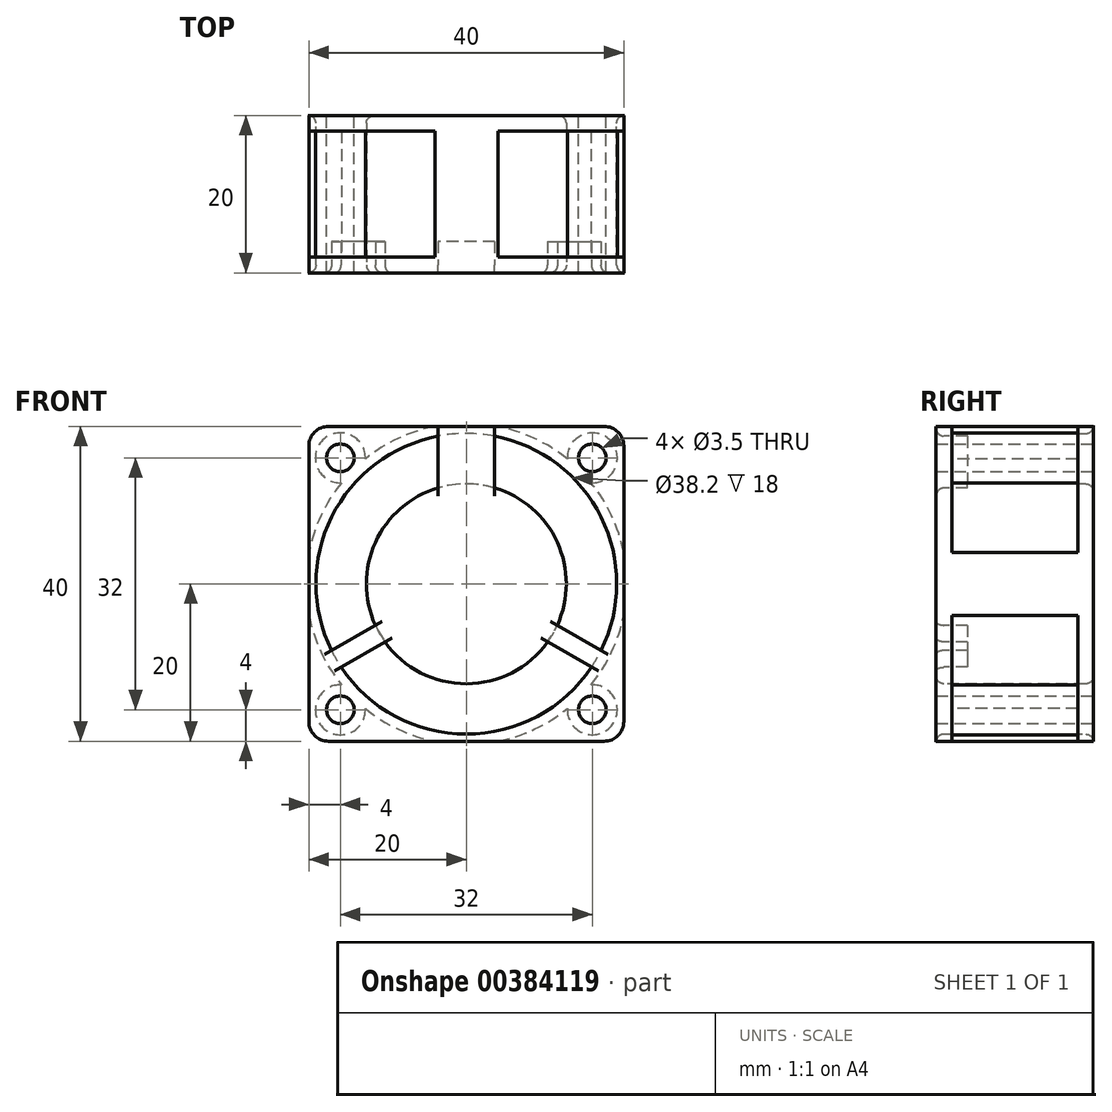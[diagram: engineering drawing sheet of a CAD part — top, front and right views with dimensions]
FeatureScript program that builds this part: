
annotation { "Feature Type Name" : "Feature", "Feature Type Description" : "" }
export const myFeature = defineFeature(function(context is Context, id is Id, definition is map)
    precondition{}
    {
        {
            var Q0;
            Q0=qCreatedBy(makeId("Front.planeOp"),FACE);
            var sketch = newSketch(context, id + "F0", { "sketchPlane" : qUnion([Q0])});
            skLineSegment(sketch, "E0.bottom", {"start": v(-20, 20) * mm, "end": v(20, 20) * mm});
            skLineSegment(sketch, "E0.top", {"start": v(-20, -20) * mm, "end": v(20, -20) * mm});
            skLineSegment(sketch, "E0.left", {"start": v(-20, 20) * mm, "end": v(-20, -20) * mm});
            skLineSegment(sketch, "E0.right", {"start": v(20, 20) * mm, "end": v(20, -20) * mm});
            skLineSegment(sketch, "E1", {"start": v(0, 22.42) * mm, "end": v(0, -25.75) * mm, "construction": true});
            skLineSegment(sketch, "E2", {"start": v(-21.61, 0) * mm, "end": v(23.43, 0) * mm, "construction": true});
            skLineSegment(sketch, "E3", {"start": v(-20.42, 20.42) * mm, "end": v(24.04, -24.04) * mm, "construction": true});
            skLineSegment(sketch, "E4", {"start": v(22.41, 22.41) * mm, "end": v(-20.4, -20.4) * mm, "construction": true});
            skCircle(sketch, "E5", {"center": v(-16, 16) * mm, "radius": 1.75 * mm});
            skCircle(sketch, "E6", {"center": v(16, 16) * mm, "radius": 1.75 * mm});
            skCircle(sketch, "E7", {"center": v(16, -16) * mm, "radius": 1.75 * mm});
            skCircle(sketch, "E8", {"center": v(-16, -16) * mm, "radius": 1.75 * mm});
            skCircle(sketch, "E9", {"center": v(0, 0) * mm, "radius": 19.1 * mm});
            skSolve(sketch);
        }
        {
            var Q0;
            Q0=qSketchRegion(id+"F0",true);
            extrude(context, id + "F1", {"entities" : qUnion([Q0]), "offsetDistance" : 25 * mm, "depth" : 20 * mm, "symmetric" : true});
        }
        {
            var Q0;
            Q0=qCreatedBy(makeId("Front.planeOp"),FACE);
            var sketch = newSketch(context, id + "F2", { "sketchPlane" : qUnion([Q0])});
            skArc(sketch, "E10", {"start": v(-12.83, 15.86) * mm, "mid": v(-18.25, 18.25) * mm, "end": v(-15.86, 12.83) * mm});
            skArc(sketch, "E11", {"start": v(-15.86, 12.83) * mm, "mid": v(-18.46, 8.67) * mm, "end": v(-20, 4) * mm});
            skLineSegment(sketch, "E12", {"start": v(20.4, 20.4) * mm, "end": v(4, 20.4) * mm});
            skLineSegment(sketch, "E13", {"start": v(-20.4, 20.4) * mm, "end": v(-20.4, 4) * mm});
            skLineSegment(sketch, "E14", {"start": v(-20.4, -20.4) * mm, "end": v(-4, -20.4) * mm});
            skLineSegment(sketch, "E15", {"start": v(20.4, -20.4) * mm, "end": v(20.4, -4) * mm});
            skArc(sketch, "E16", {"start": v(15.86, 12.83) * mm, "mid": v(18.25, 18.25) * mm, "end": v(12.83, 15.86) * mm});
            skArc(sketch, "E17", {"start": v(12.83, -15.86) * mm, "mid": v(18.25, -18.25) * mm, "end": v(15.86, -12.83) * mm});
            skArc(sketch, "E18", {"start": v(-15.86, -12.83) * mm, "mid": v(-18.25, -18.25) * mm, "end": v(-12.83, -15.86) * mm});
            skArc(sketch, "E19.trimOffspring", {"start": v(12.83, 15.86) * mm, "mid": v(8.67, 18.46) * mm, "end": v(4, 20) * mm});
            skArc(sketch, "E20.trimOffspring", {"start": v(15.86, -12.83) * mm, "mid": v(18.46, -8.67) * mm, "end": v(20, -4) * mm});
            skArc(sketch, "E21.trimOffspring", {"start": v(-12.83, -15.86) * mm, "mid": v(-8.67, -18.46) * mm, "end": v(-4, -20) * mm});
            skLineSegment(sketch, "E22", {"start": v(-20, 4) * mm, "end": v(-20.4, 4) * mm});
            skLineSegment(sketch, "E23", {"start": v(-20, -4) * mm, "end": v(-20.4, -4) * mm});
            skLineSegment(sketch, "E24", {"start": v(20, -4) * mm, "end": v(20.4, -4) * mm});
            skLineSegment(sketch, "E25", {"start": v(-4, -20) * mm, "end": v(-4, -20.4) * mm});
            skArc(sketch, "E26.trimOffspring", {"start": v(-20, -4) * mm, "mid": v(-18.46, -8.67) * mm, "end": v(-15.86, -12.83) * mm});
            skLineSegment(sketch, "E27.trimOffspring", {"start": v(-20.4, -4) * mm, "end": v(-20.4, -20.4) * mm});
            skLineSegment(sketch, "E28.trimOffspring", {"start": v(4, -20.4) * mm, "end": v(20.4, -20.4) * mm});
            skArc(sketch, "E29.trimOffspring", {"start": v(4, -20) * mm, "mid": v(8.67, -18.46) * mm, "end": v(12.83, -15.86) * mm});
            skLineSegment(sketch, "E30.trimOffspring", {"start": v(20.4, 4) * mm, "end": v(20.4, 20.4) * mm});
            skArc(sketch, "E31.trimOffspring", {"start": v(20, 4) * mm, "mid": v(18.46, 8.67) * mm, "end": v(15.86, 12.83) * mm});
            skLineSegment(sketch, "E32.trimOffspring", {"start": v(-4, 20.4) * mm, "end": v(-20.4, 20.4) * mm});
            skArc(sketch, "E33.trimOffspring", {"start": v(-4, 20) * mm, "mid": v(-8.67, 18.46) * mm, "end": v(-12.83, 15.86) * mm});
            skLineSegment(sketch, "E34", {"start": v(4, 20.4) * mm, "end": v(4, 20) * mm});
            skLineSegment(sketch, "E35", {"start": v(-4, 20.4) * mm, "end": v(-4, 20) * mm});
            skLineSegment(sketch, "E36", {"start": v(20, 4) * mm, "end": v(20.4, 4) * mm});
            skLineSegment(sketch, "E37", {"start": v(4, -20.4) * mm, "end": v(4, -20) * mm});
            skSolve(sketch);
        }
        {
            var Q0;
            Q0=qSketchRegion(id+"F2",true);
            extrude(context, id + "F3", {"entities" : qUnion([Q0]), "operationType" : NewBodyOperationType.REMOVE, "oppositeDirection" : true, "offsetDistance" : 25 * mm, "depth" : 16 * mm, "symmetric" : true});
        }
        {
            var Q0;
            {var subQ0=sQuery(id+"F0.wireOp",EDGE,"E0.bottom");var subQ1=sQuery(id+"F0.wireOp",EDGE,"E0.right");Q0=makeQuery(id+"F3.boolean.opBoolean","SPLIT",EDGE,{"disambiguationData":[TD([makeQuery(id+"F3.opExtrude","CAP_FACE",FACE,{"disambiguationData":[OSD([sQuery(id+"F2.wireOp",EDGE,"E12"),sQuery(id+"F2.wireOp",EDGE,"E16"),sQuery(id+"F2.wireOp",EDGE,"E19.trimOffspring"),sQuery(id+"F2.wireOp",EDGE,"5qj6X1HE-5dRS-yjT4-1pPR-XCu9oSXyVZGm"),sQuery(id+"F2.wireOp",EDGE,"E24"),sQuery(id+"F2.wireOp",EDGE,"E30.trimOffspring"),sQuery(id+"F2.wireOp",EDGE,"E31.trimOffspring")])],"isStart":true})])],"derivedFrom":makeQuery(id+"F1.opExtrude","SWEPT_EDGE",EDGE,{"disambiguationData":[OSD([subQ0,subQ1])]})});}
            var Q1;
            {var subQ0=sQuery(id+"F0.wireOp",EDGE,"E0.bottom");var subQ1=sQuery(id+"F0.wireOp",EDGE,"E0.right");Q1=makeQuery(id+"F3.boolean.opBoolean","SPLIT",EDGE,{"disambiguationData":[TD([makeQuery(id+"F3.opExtrude","CAP_FACE",FACE,{"disambiguationData":[OSD([sQuery(id+"F2.wireOp",EDGE,"E12"),sQuery(id+"F2.wireOp",EDGE,"E16"),sQuery(id+"F2.wireOp",EDGE,"E19.trimOffspring"),sQuery(id+"F2.wireOp",EDGE,"5qj6X1HE-5dRS-yjT4-1pPR-XCu9oSXyVZGm"),sQuery(id+"F2.wireOp",EDGE,"E24"),sQuery(id+"F2.wireOp",EDGE,"E30.trimOffspring"),sQuery(id+"F2.wireOp",EDGE,"E31.trimOffspring")])],"isStart":false})])],"derivedFrom":makeQuery(id+"F1.opExtrude","SWEPT_EDGE",EDGE,{"disambiguationData":[OSD([subQ0,subQ1])]})});}
            var Q2;
            {var subQ0=sQuery(id+"F0.wireOp",EDGE,"E0.right");var subQ1=sQuery(id+"F0.wireOp",EDGE,"E0.top");Q2=makeQuery(id+"F3.boolean.opBoolean","SPLIT",EDGE,{"disambiguationData":[TD([makeQuery(id+"F3.opExtrude","CAP_FACE",FACE,{"disambiguationData":[OSD([sQuery(id+"F2.wireOp",EDGE,"E15"),sQuery(id+"F2.wireOp",EDGE,"E17"),sQuery(id+"F2.wireOp",EDGE,"E20.trimOffspring"),sQuery(id+"F2.wireOp",EDGE,"E24"),sQuery(id+"F2.wireOp",EDGE,"E25"),sQuery(id+"F2.wireOp",EDGE,"E28.trimOffspring"),sQuery(id+"F2.wireOp",EDGE,"E29.trimOffspring")])],"isStart":true})])],"derivedFrom":makeQuery(id+"F1.opExtrude","SWEPT_EDGE",EDGE,{"disambiguationData":[OSD([subQ1,subQ0])]})});}
            var Q3;
            {var subQ0=sQuery(id+"F0.wireOp",EDGE,"E0.right");var subQ1=sQuery(id+"F0.wireOp",EDGE,"E0.top");Q3=makeQuery(id+"F3.boolean.opBoolean","SPLIT",EDGE,{"disambiguationData":[TD([makeQuery(id+"F3.opExtrude","CAP_FACE",FACE,{"disambiguationData":[OSD([sQuery(id+"F2.wireOp",EDGE,"E15"),sQuery(id+"F2.wireOp",EDGE,"E17"),sQuery(id+"F2.wireOp",EDGE,"E20.trimOffspring"),sQuery(id+"F2.wireOp",EDGE,"E24"),sQuery(id+"F2.wireOp",EDGE,"E25"),sQuery(id+"F2.wireOp",EDGE,"E28.trimOffspring"),sQuery(id+"F2.wireOp",EDGE,"E29.trimOffspring")])],"isStart":false})])],"derivedFrom":makeQuery(id+"F1.opExtrude","SWEPT_EDGE",EDGE,{"disambiguationData":[OSD([subQ1,subQ0])]})});}
            var Q4;
            {var subQ0=sQuery(id+"F0.wireOp",EDGE,"E0.bottom");var subQ1=sQuery(id+"F0.wireOp",EDGE,"E0.left");Q4=makeQuery(id+"F3.boolean.opBoolean","SPLIT",EDGE,{"disambiguationData":[TD([makeQuery(id+"F3.opExtrude","CAP_FACE",FACE,{"disambiguationData":[OSD([sQuery(id+"F2.wireOp",EDGE,"E10"),sQuery(id+"F2.wireOp",EDGE,"E11"),sQuery(id+"F2.wireOp",EDGE,"E13"),sQuery(id+"F2.wireOp",EDGE,"pvrkBk7z-V1rM-OS9Q-dIUC-16UQzA1z2bkd"),sQuery(id+"F2.wireOp",EDGE,"E22"),sQuery(id+"F2.wireOp",EDGE,"E32.trimOffspring"),sQuery(id+"F2.wireOp",EDGE,"E33.trimOffspring")])],"isStart":true})])],"derivedFrom":makeQuery(id+"F1.opExtrude","SWEPT_EDGE",EDGE,{"disambiguationData":[OSD([subQ0,subQ1])]})});}
            var Q5;
            {var subQ0=sQuery(id+"F0.wireOp",EDGE,"E0.bottom");var subQ1=sQuery(id+"F0.wireOp",EDGE,"E0.left");Q5=makeQuery(id+"F3.boolean.opBoolean","SPLIT",EDGE,{"disambiguationData":[TD([makeQuery(id+"F3.opExtrude","CAP_FACE",FACE,{"disambiguationData":[OSD([sQuery(id+"F2.wireOp",EDGE,"E10"),sQuery(id+"F2.wireOp",EDGE,"E11"),sQuery(id+"F2.wireOp",EDGE,"E13"),sQuery(id+"F2.wireOp",EDGE,"pvrkBk7z-V1rM-OS9Q-dIUC-16UQzA1z2bkd"),sQuery(id+"F2.wireOp",EDGE,"E22"),sQuery(id+"F2.wireOp",EDGE,"E32.trimOffspring"),sQuery(id+"F2.wireOp",EDGE,"E33.trimOffspring")])],"isStart":false})])],"derivedFrom":makeQuery(id+"F1.opExtrude","SWEPT_EDGE",EDGE,{"disambiguationData":[OSD([subQ0,subQ1])]})});}
            var Q6;
            {var subQ0=sQuery(id+"F0.wireOp",EDGE,"E0.left");var subQ1=sQuery(id+"F0.wireOp",EDGE,"E0.top");Q6=makeQuery(id+"F3.boolean.opBoolean","SPLIT",EDGE,{"disambiguationData":[TD([makeQuery(id+"F3.opExtrude","CAP_FACE",FACE,{"disambiguationData":[OSD([sQuery(id+"F2.wireOp",EDGE,"E14"),sQuery(id+"F2.wireOp",EDGE,"E18"),sQuery(id+"F2.wireOp",EDGE,"E21.trimOffspring"),sQuery(id+"F2.wireOp",EDGE,"E23"),sQuery(id+"F2.wireOp",EDGE,"E25"),sQuery(id+"F2.wireOp",EDGE,"E26.trimOffspring"),sQuery(id+"F2.wireOp",EDGE,"E27.trimOffspring")])],"isStart":false})])],"derivedFrom":makeQuery(id+"F1.opExtrude","SWEPT_EDGE",EDGE,{"disambiguationData":[OSD([subQ1,subQ0])]})});}
            var Q7;
            {var subQ0=sQuery(id+"F0.wireOp",EDGE,"E0.left");var subQ1=sQuery(id+"F0.wireOp",EDGE,"E0.top");Q7=makeQuery(id+"F3.boolean.opBoolean","SPLIT",EDGE,{"disambiguationData":[TD([makeQuery(id+"F3.opExtrude","CAP_FACE",FACE,{"disambiguationData":[OSD([sQuery(id+"F2.wireOp",EDGE,"E14"),sQuery(id+"F2.wireOp",EDGE,"E18"),sQuery(id+"F2.wireOp",EDGE,"E21.trimOffspring"),sQuery(id+"F2.wireOp",EDGE,"E23"),sQuery(id+"F2.wireOp",EDGE,"E25"),sQuery(id+"F2.wireOp",EDGE,"E26.trimOffspring"),sQuery(id+"F2.wireOp",EDGE,"E27.trimOffspring")])],"isStart":true})])],"derivedFrom":makeQuery(id+"F1.opExtrude","SWEPT_EDGE",EDGE,{"disambiguationData":[OSD([subQ1,subQ0])]})});}
            fillet(context, id + "F4", {"entities" : qUnion([Q0, Q1, Q2, Q3, Q4, Q5, Q6, Q7]), "radius" : 2.5 * mm, "tangentPropagation" : true, "allowEdgeOverflow" : false});
        }
        {
            var Q0;
            Q0=makeQuery(id+"F1.opExtrude","CAP_FACE",FACE,{"disambiguationData":[OSD([sQuery(id+"F0.wireOp",EDGE,"E0.bottom"),sQuery(id+"F0.wireOp",EDGE,"E0.top"),sQuery(id+"F0.wireOp",EDGE,"E0.left"),sQuery(id+"F0.wireOp",EDGE,"E0.right"),sQuery(id+"F0.wireOp",EDGE,"E5"),sQuery(id+"F0.wireOp",EDGE,"E6"),sQuery(id+"F0.wireOp",EDGE,"E7"),sQuery(id+"F0.wireOp",EDGE,"E8"),sQuery(id+"F0.wireOp",EDGE,"E9")])],"isStart":false});
            var sketch = newSketch(context, id + "F5", { "sketchPlane" : qUnion([Q0])});
            skArc(sketch, "E38", {"start": v(-3.6, 12.18) * mm, "mid": v(-11.55, 5.27) * mm, "end": v(-11.56, -5.26) * mm});
            skLineSegment(sketch, "E39", {"start": v(0, 0) * mm, "end": v(0, 20.9) * mm, "construction": true});
            skLineSegment(sketch, "E40.1.0", {"start": v(0, 0) * mm, "end": v(-18.1, -10.45) * mm, "construction": true});
            skLineSegment(sketch, "E40.2.0", {"start": v(0, 0) * mm, "end": v(18.1, -10.45) * mm, "construction": true});
            skLineSegment(sketch, "E41", {"start": v(-3.6, 18.76) * mm, "end": v(-3.6, 12.18) * mm});
            skLineSegment(sketch, "E42", {"start": v(3.6, 12.18) * mm, "end": v(3.6, 18.76) * mm});
            skArc(sketch, "E43", {"start": v(-3.6, 18.76) * mm, "mid": v(0, 19.1) * mm, "end": v(3.6, 18.76) * mm});
            skLineSegment(sketch, "E44", {"start": v(-11.56, -5.26) * mm, "end": v(-17.12, -8.47) * mm});
            skLineSegment(sketch, "E45", {"start": v(-10.33, -7.38) * mm, "end": v(-15.9, -10.6) * mm});
            skLineSegment(sketch, "E46", {"start": v(10.33, -7.38) * mm, "end": v(15.9, -10.6) * mm});
            skLineSegment(sketch, "E47", {"start": v(11.56, -5.26) * mm, "end": v(17.12, -8.47) * mm});
            skArc(sketch, "E48.trimOffspring", {"start": v(-10.33, -7.38) * mm, "mid": v(0, -12.7) * mm, "end": v(10.33, -7.38) * mm});
            skArc(sketch, "E49.trimOffspring", {"start": v(11.56, -5.26) * mm, "mid": v(11.55, 5.27) * mm, "end": v(3.6, 12.18) * mm});
            skArc(sketch, "E50", {"start": v(-17.12, -8.47) * mm, "mid": v(-16.54, -9.55) * mm, "end": v(-15.9, -10.6) * mm});
            skArc(sketch, "E51", {"start": v(17.12, -8.47) * mm, "mid": v(16.54, -9.55) * mm, "end": v(15.9, -10.6) * mm});
            skSolve(sketch);
        }
        {
            var Q0;
            Q0=qSketchRegion(id+"F5",true);
            extrude(context, id + "F6", {"entities" : qUnion([Q0]), "operationType" : NewBodyOperationType.ADD, "oppositeDirection" : true, "depth" : 4 * mm});
        }
        {
            var Q0;
            Q0=qCreatedBy(makeId("Right.planeOp"),FACE);
            var sketch = newSketch(context, id + "F7", { "sketchPlane" : qUnion([Q0])});
            skLineSegment(sketch, "E52", {"start": v(10, 0) * mm, "end": v(10, 12.7) * mm});
            skLineSegment(sketch, "E53", {"start": v(10, 12.7) * mm, "end": v(-8, 12.7) * mm});
            skLineSegment(sketch, "E54", {"start": v(-8, 12.7) * mm, "end": v(-8, 0) * mm});
            skLineSegment(sketch, "E55", {"start": v(-8, 0) * mm, "end": v(10, 0) * mm});
            skLineSegment(sketch, "E56", {"start": v(-15.88, 0) * mm, "end": v(18.33, 0) * mm, "construction": true});
            skSolve(sketch);
        }
        {
            var Q0;
            Q0=qSketchRegion(id+"F7",true);
            var Q1;
            Q1=sQuery(id+"F7.wireOp",EDGE,"E56");
            revolve(context, id + "F8", {"operationType" : NewBodyOperationType.ADD, "entities" : qUnion([Q0]), "axis" : qUnion([Q1]), "revolveType" : RevolveType.FULL});
        }
        {
            var Q0;
            Q0=makeQuery(id+"F8.opRevolve","SWEPT_EDGE",EDGE,{"disambiguationData":[OSD([sQuery(id+"F7.wireOp",EDGE,"E52"),sQuery(id+"F7.wireOp",EDGE,"E53")])]});
            var Q1;
            Q1=makeQuery(id+"F6.opExtrude","CAP_EDGE",EDGE,{"disambiguationData":[OSD([sQuery(id+"F5.wireOp",EDGE,"E49.trimOffspring")])],"isStart":true});
            var Q2;
            Q2=makeQuery(id+"F6.opExtrude","CAP_EDGE",EDGE,{"disambiguationData":[OSD([sQuery(id+"F5.wireOp",EDGE,"E38")])],"isStart":true});
            var Q3;
            Q3=makeQuery(id+"F6.opExtrude","CAP_EDGE",EDGE,{"disambiguationData":[OSD([sQuery(id+"F5.wireOp",EDGE,"E48.trimOffspring")])],"isStart":true});
            var Q4;
            {var subQ0=sQuery(id+"F5.wireOp",EDGE,"E41");var subQ1=sQuery(id+"F0.wireOp",EDGE,"E9");Q4=makeQuery(id+"F6.boolean.opBoolean","SPLIT",EDGE,{"disambiguationData":[TD([makeQuery(id+"F6.opExtrude","SWEPT_FACE",FACE,{"disambiguationData":[OSD([subQ0])]})])],"derivedFrom":makeQuery(id+"F1.opExtrude","CAP_EDGE",EDGE,{"disambiguationData":[OSD([subQ1])],"isStart":false})});}
            var Q5;
            {var subQ1=sQuery(id+"F5.wireOp",EDGE,"E42");var subQ2=sQuery(id+"F0.wireOp",EDGE,"E9");Q5=makeQuery(id+"F6.boolean.opBoolean","SPLIT",EDGE,{"disambiguationData":[TD([makeQuery(id+"F6.opExtrude","SWEPT_FACE",FACE,{"disambiguationData":[OSD([subQ1])]})])],"derivedFrom":makeQuery(id+"F1.opExtrude","CAP_EDGE",EDGE,{"disambiguationData":[OSD([subQ2])],"isStart":false})});}
            var Q6;
            {var subQ1=sQuery(id+"F5.wireOp",EDGE,"E45");var subQ2=sQuery(id+"F0.wireOp",EDGE,"E9");Q6=makeQuery(id+"F6.boolean.opBoolean","SPLIT",EDGE,{"disambiguationData":[TD([makeQuery(id+"F6.opExtrude","SWEPT_FACE",FACE,{"disambiguationData":[OSD([subQ1])]})])],"derivedFrom":makeQuery(id+"F1.opExtrude","CAP_EDGE",EDGE,{"disambiguationData":[OSD([subQ2])],"isStart":false})});}
            var Q7;
            Q7=makeQuery(id+"F1.opExtrude","CAP_EDGE",EDGE,{"disambiguationData":[OSD([sQuery(id+"F0.wireOp",EDGE,"E9")])],"isStart":true});
            fillet(context, id + "F9", {"entities" : qUnion([Q0, Q1, Q2, Q3, Q4, Q5, Q6, Q7]), "radius" : 1 * mm, "tangentPropagation" : true, "allowEdgeOverflow" : false});
        }
    });
